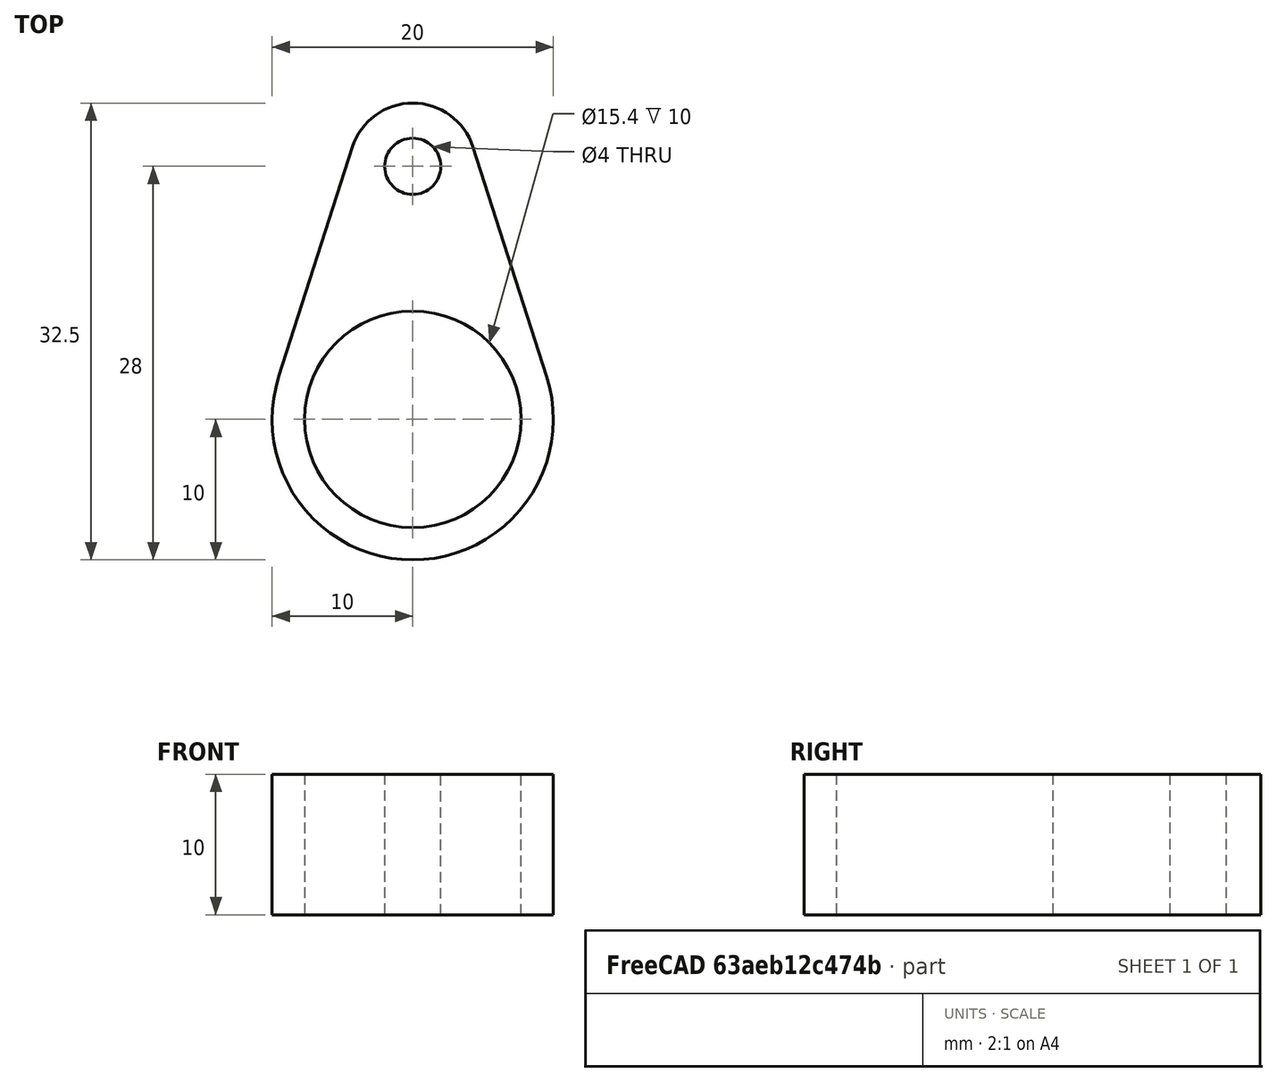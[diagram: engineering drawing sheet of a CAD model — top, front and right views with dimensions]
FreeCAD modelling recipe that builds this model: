
FCSTD DOCUMENT  (FreeCAD 0.16R)
Label: CableStop15mm
License: All rights reserved
LicenseURL: http://en.wikipedia.org/wiki/All_rights_reserved
objects: Sketcher::SketchObject×1, PartDesign::Pad×1, Mesh::Feature×1
note: 3 computed .brp shape members not serialized (recipe doc carries the construction recipe); baked Part::Feature solids carry a one-line shape summary decoded from their .brp

FEATURE [Sketcher::SketchObject] Sketch
  sketch-geometry (6):
    g0: Circle CenterX=0 CenterY=18 CenterZ=0 NormalX=0 NormalY=0 NormalZ=1 Radius=2
    g1: Circle CenterX=0 CenterY=0 CenterZ=0 NormalX=0 NormalY=0 NormalZ=1 Radius=7.7
    g2: LineSegment StartX=-9.52174 StartY=3.05555 StartZ=0 EndX=-4.28478 EndY=19.375 EndZ=0
    g3: LineSegment StartX=4.28478 StartY=19.375 StartZ=0 EndX=9.52174 EndY=3.05555 EndZ=0
    g4: ArcOfCircle CenterX=0 CenterY=18 CenterZ=0 NormalX=0 NormalY=0 NormalZ=1 Radius=4.5 StartAngle=0.310525 EndAngle=2.83107
    g5: ArcOfCircle CenterX=0 CenterY=0 CenterZ=0 NormalX=0 NormalY=0 NormalZ=1 Radius=10 StartAngle=2.83107 EndAngle=6.59371
  constraints (17):
    c: Coincident(g1,g-1)
    c: Radius(g1) = 7.7
    c: PointOnObject(g0,g-2)
    c: Distance(g-1,g0) = 18
    c: Radius(g0) = 2
    c: Coincident(g4,g0)
    c: Coincident(g4,g2)
    c: Coincident(g4,g3)
    c: Coincident(g5,g-1)
    c: Coincident(g5,g3)
    c: Coincident(g5,g2)
    c: Tangent(g5,g3)
    c: Tangent(g5,g2)
    c: Tangent(g2,g4)
    c: Tangent(g3,g4)
    c: Radius(g5) = 10
    c: Radius(g4) = 4.5
FEATURE [PartDesign::Pad] Pad
  Length = 10
  Length2 = 100
  Sketch = -> Sketch
  Type = 0
FEATURE [Mesh::Feature] Mesh  label="Pad (Meshed)"
